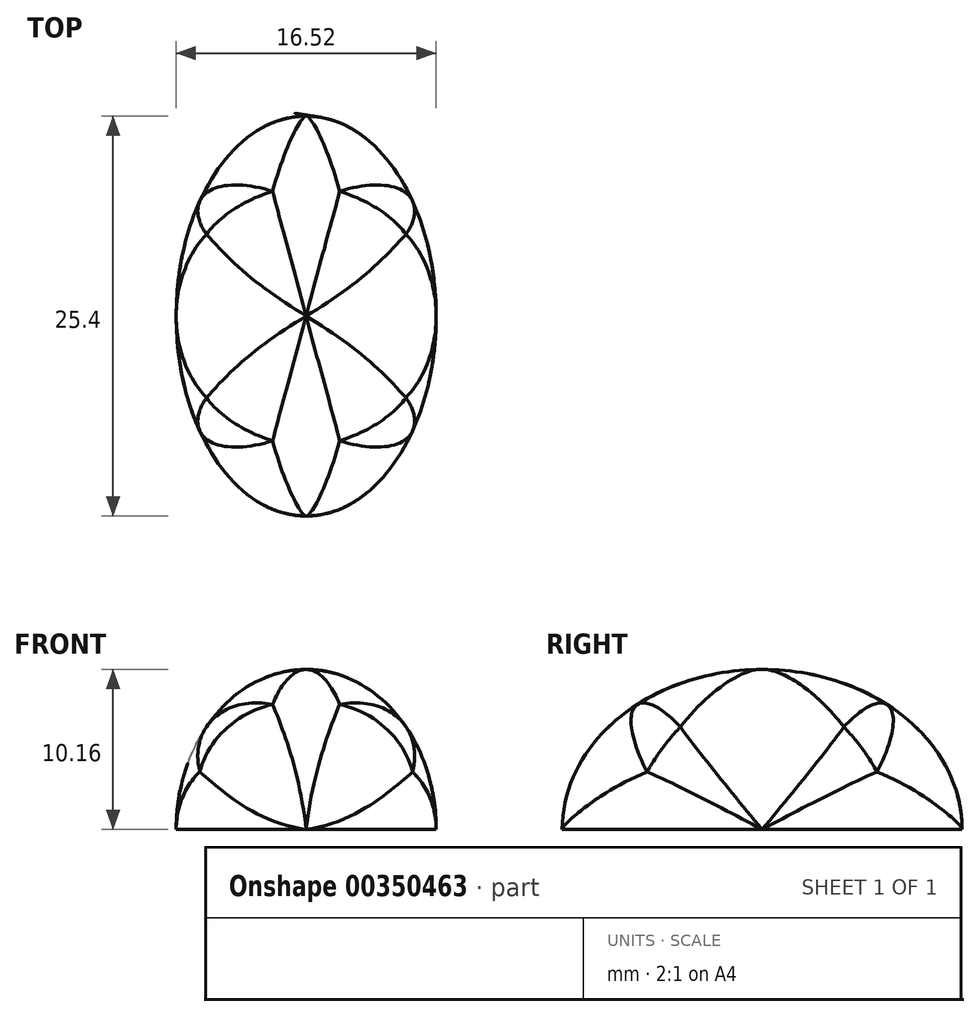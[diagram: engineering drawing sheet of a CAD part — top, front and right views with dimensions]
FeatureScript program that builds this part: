
annotation { "Feature Type Name" : "Feature", "Feature Type Description" : "" }
export const myFeature = defineFeature(function(context is Context, id is Id, definition is map)
    precondition{}
    {
        {
            var Q0;
            Q0=qCreatedBy(makeId("Top.planeOp"),FACE);
            var sketch = newSketch(context, id + "F0", { "sketchPlane" : qUnion([Q0])});
            skEllipse(sketch, "E0", {"center": v(0, 0) * mm, "majorRadius": 12.7 * mm, "minorRadius": 8.26 * mm, "majorAxis": v(0, 1)});
            skSolve(sketch);
        }
        {
            var Q0;
            Q0=makeQuery(id+"F0.imprint","IMPRINT",FACE,{"disambiguationData":[TD([[makeQuery(id+"F0.imprint","IMPRINT",EDGE,{"derivedFrom":sQuery(id+"F0.wireOp",EDGE,"E0")}),1.0]])]});
            extrude(context, id + "F1", {"entities" : qUnion([Q0]), "depth" : 10.16 * mm});
        }
        {
            var Q0;
            Q0=qCreatedBy(makeId("Front.planeOp"),FACE);
            var sketch = newSketch(context, id + "F2", { "sketchPlane" : qUnion([Q0])});
            skEllipticalArc(sketch, "E1", {});
            skLineSegment(sketch, "E2", {"start": v(8.26, 0) * mm, "end": v(8.26, 12.35) * mm});
            skLineSegment(sketch, "E3", {"start": v(-8.26, 0) * mm, "end": v(-8.26, 12.73) * mm});
            skLineSegment(sketch, "E4", {"start": v(-8.26, 12.73) * mm, "end": v(8.26, 12.35) * mm});
            const initialGuessF2  = {"E1": [0, 0, 0, 1, 0.01016, 0.008255, 4.71238898038469, 1.5707963267948966]};
            skSetInitialGuess(sketch, initialGuessF2);
            skSolve(sketch);
        }
        {
            var Q0;
            Q0=qSketchRegion(id+"F2",true);
            extrude(context, id + "F3", {"entities" : qUnion([Q0]), "operationType" : NewBodyOperationType.REMOVE, "endBound" : BoundingType.SYMMETRIC, "oppositeDirection" : true, "depth" : 25.4 * mm});
        }
        {
            var Q0;
            Q0=qCreatedBy(makeId("Right.planeOp"),FACE);
            var sketch = newSketch(context, id + "F4", { "sketchPlane" : qUnion([Q0])});
            skEllipticalArc(sketch, "E5", {});
            skLineSegment(sketch, "E6", {"start": v(12.7, 0) * mm, "end": v(12.7, 13.18) * mm});
            skLineSegment(sketch, "E7", {"start": v(-12.7, 0) * mm, "end": v(-12.7, 12.71) * mm});
            skLineSegment(sketch, "E8", {"start": v(-12.7, 12.71) * mm, "end": v(12.7, 13.18) * mm});
            const initialGuessF4  = {"E5": [0, 0, 0, 1, 0.01016, 0.0127, 4.71238898038469, 1.5707963267948966]};
            skSetInitialGuess(sketch, initialGuessF4);
            skSolve(sketch);
        }
        {
            var Q0;
            Q0=makeQuery(id+"F4.imprint","IMPRINT",FACE,{"disambiguationData":[TD([[makeQuery(id+"F4.imprint","IMPRINT",EDGE,{"derivedFrom":sQuery(id+"F4.wireOp",EDGE,"E5")}),-1.0]])]});
            extrude(context, id + "F5", {"entities" : qUnion([Q0]), "operationType" : NewBodyOperationType.REMOVE, "endBound" : BoundingType.SYMMETRIC, "oppositeDirection" : true, "depth" : 25.4 * mm});
        }
        {
            var Q0;
            Q0=makeQuery(id+"F5.boolean.opBoolean","INTERSECT",EDGE,{"disambiguationData":[OD(0.0)],"derivedFrom":[makeQuery(id+"F3.boolean.opBoolean","SPLIT",FACE,{"disambiguationData":[OD(0.0)],"derivedFrom":makeQuery(id+"F1.opExtrude","SWEPT_FACE",FACE,{"disambiguationData":[OSD([sQuery(id+"F0.wireOp",EDGE,"E0")])]})}),makeQuery(id+"F5.opExtrude","SWEPT_FACE",FACE,{"disambiguationData":[OSD([sQuery(id+"F4.wireOp",EDGE,"E5")])]})]});
            var Q1;
            Q1=makeQuery(id+"F5.boolean.opBoolean","SPLIT",EDGE,{"disambiguationData":[OD(0.0)],"derivedFrom":makeQuery(id+"F3.boolean.opBoolean","INTERSECT",EDGE,{"disambiguationData":[OD(0.0)],"derivedFrom":[makeQuery(id+"F1.opExtrude","SWEPT_FACE",FACE,{"disambiguationData":[OSD([sQuery(id+"F0.wireOp",EDGE,"E0")])]}),makeQuery(id+"F3.opExtrude","SWEPT_FACE",FACE,{"disambiguationData":[OSD([sQuery(id+"F2.wireOp",EDGE,"E1")])]})]})});
            var Q2;
            Q2=makeQuery(id+"F5.boolean.opBoolean","INTERSECT",EDGE,{"disambiguationData":[OD(0.0)],"derivedFrom":[makeQuery(id+"F3.boolean.opBoolean","COPY",FACE,{"derivedFrom":makeQuery(id+"F3.opExtrude","SWEPT_FACE",FACE,{"disambiguationData":[OSD([sQuery(id+"F2.wireOp",EDGE,"E1")])]})}),makeQuery(id+"F5.opExtrude","SWEPT_FACE",FACE,{"disambiguationData":[OSD([sQuery(id+"F4.wireOp",EDGE,"E5")])]})]});
            fillet(context, id + "F6", {"entities" : qUnion([Q0, Q1, Q2]), "radius" : 5.08 * mm, "tangentPropagation" : true, "allowEdgeOverflow" : false});
        }
        {
            var Q0;
            Q0=makeQuery(id+"F5.boolean.opBoolean","INTERSECT",EDGE,{"disambiguationData":[OD(0.0)],"derivedFrom":[makeQuery(id+"F3.boolean.opBoolean","SPLIT",FACE,{"disambiguationData":[OD(1.0)],"derivedFrom":makeQuery(id+"F1.opExtrude","SWEPT_FACE",FACE,{"disambiguationData":[OSD([sQuery(id+"F0.wireOp",EDGE,"E0")])]})}),makeQuery(id+"F5.opExtrude","SWEPT_FACE",FACE,{"disambiguationData":[OSD([sQuery(id+"F4.wireOp",EDGE,"E5")])]})]});
            var Q1;
            Q1=makeQuery(id+"F5.boolean.opBoolean","INTERSECT",EDGE,{"disambiguationData":[OD(2.0)],"derivedFrom":[makeQuery(id+"F3.boolean.opBoolean","COPY",FACE,{"derivedFrom":makeQuery(id+"F3.opExtrude","SWEPT_FACE",FACE,{"disambiguationData":[OSD([sQuery(id+"F2.wireOp",EDGE,"E1")])]})}),makeQuery(id+"F5.opExtrude","SWEPT_FACE",FACE,{"disambiguationData":[OSD([sQuery(id+"F4.wireOp",EDGE,"E5")])]})]});
            var Q2;
            Q2=makeQuery(id+"F5.boolean.opBoolean","SPLIT",EDGE,{"disambiguationData":[OD(0.0)],"derivedFrom":makeQuery(id+"F3.boolean.opBoolean","INTERSECT",EDGE,{"disambiguationData":[OD(1.0)],"derivedFrom":[makeQuery(id+"F1.opExtrude","SWEPT_FACE",FACE,{"disambiguationData":[OSD([sQuery(id+"F0.wireOp",EDGE,"E0")])]}),makeQuery(id+"F3.opExtrude","SWEPT_FACE",FACE,{"disambiguationData":[OSD([sQuery(id+"F2.wireOp",EDGE,"E1")])]})]})});
            fillet(context, id + "F7", {"entities" : qUnion([Q0, Q1, Q2]), "radius" : 5.08 * mm, "tangentPropagation" : true, "allowEdgeOverflow" : false});
        }
        {
            var Q0;
            Q0=makeQuery(id+"F5.boolean.opBoolean","INTERSECT",EDGE,{"disambiguationData":[OD(3.0)],"derivedFrom":[makeQuery(id+"F3.boolean.opBoolean","COPY",FACE,{"derivedFrom":makeQuery(id+"F3.opExtrude","SWEPT_FACE",FACE,{"disambiguationData":[OSD([sQuery(id+"F2.wireOp",EDGE,"E1")])]})}),makeQuery(id+"F5.opExtrude","SWEPT_FACE",FACE,{"disambiguationData":[OSD([sQuery(id+"F4.wireOp",EDGE,"E5")])]})]});
            var Q1;
            Q1=makeQuery(id+"F5.boolean.opBoolean","SPLIT",EDGE,{"disambiguationData":[OD(1.0)],"derivedFrom":makeQuery(id+"F3.boolean.opBoolean","INTERSECT",EDGE,{"disambiguationData":[OD(1.0)],"derivedFrom":[makeQuery(id+"F1.opExtrude","SWEPT_FACE",FACE,{"disambiguationData":[OSD([sQuery(id+"F0.wireOp",EDGE,"E0")])]}),makeQuery(id+"F3.opExtrude","SWEPT_FACE",FACE,{"disambiguationData":[OSD([sQuery(id+"F2.wireOp",EDGE,"E1")])]})]})});
            var Q2;
            Q2=makeQuery(id+"F5.boolean.opBoolean","INTERSECT",EDGE,{"disambiguationData":[OD(1.0)],"derivedFrom":[makeQuery(id+"F3.boolean.opBoolean","SPLIT",FACE,{"disambiguationData":[OD(1.0)],"derivedFrom":makeQuery(id+"F1.opExtrude","SWEPT_FACE",FACE,{"disambiguationData":[OSD([sQuery(id+"F0.wireOp",EDGE,"E0")])]})}),makeQuery(id+"F5.opExtrude","SWEPT_FACE",FACE,{"disambiguationData":[OSD([sQuery(id+"F4.wireOp",EDGE,"E5")])]})]});
            fillet(context, id + "F8", {"entities" : qUnion([Q0, Q1, Q2]), "radius" : 5.08 * mm, "tangentPropagation" : true, "allowEdgeOverflow" : false});
        }
        {
            var Q0;
            Q0=makeQuery(id+"F5.boolean.opBoolean","INTERSECT",EDGE,{"disambiguationData":[OD(1.0)],"derivedFrom":[makeQuery(id+"F3.boolean.opBoolean","SPLIT",FACE,{"disambiguationData":[OD(0.0)],"derivedFrom":makeQuery(id+"F1.opExtrude","SWEPT_FACE",FACE,{"disambiguationData":[OSD([sQuery(id+"F0.wireOp",EDGE,"E0")])]})}),makeQuery(id+"F5.opExtrude","SWEPT_FACE",FACE,{"disambiguationData":[OSD([sQuery(id+"F4.wireOp",EDGE,"E5")])]})]});
            var Q1;
            Q1=makeQuery(id+"F5.boolean.opBoolean","INTERSECT",EDGE,{"disambiguationData":[OD(1.0)],"derivedFrom":[makeQuery(id+"F3.boolean.opBoolean","COPY",FACE,{"derivedFrom":makeQuery(id+"F3.opExtrude","SWEPT_FACE",FACE,{"disambiguationData":[OSD([sQuery(id+"F2.wireOp",EDGE,"E1")])]})}),makeQuery(id+"F5.opExtrude","SWEPT_FACE",FACE,{"disambiguationData":[OSD([sQuery(id+"F4.wireOp",EDGE,"E5")])]})]});
            var Q2;
            Q2=makeQuery(id+"F5.boolean.opBoolean","SPLIT",EDGE,{"disambiguationData":[OD(1.0)],"derivedFrom":makeQuery(id+"F3.boolean.opBoolean","INTERSECT",EDGE,{"disambiguationData":[OD(0.0)],"derivedFrom":[makeQuery(id+"F1.opExtrude","SWEPT_FACE",FACE,{"disambiguationData":[OSD([sQuery(id+"F0.wireOp",EDGE,"E0")])]}),makeQuery(id+"F3.opExtrude","SWEPT_FACE",FACE,{"disambiguationData":[OSD([sQuery(id+"F2.wireOp",EDGE,"E1")])]})]})});
            fillet(context, id + "F9", {"entities" : qUnion([Q0, Q1, Q2]), "radius" : 5.08 * mm, "tangentPropagation" : true, "allowEdgeOverflow" : false});
        }
    });
